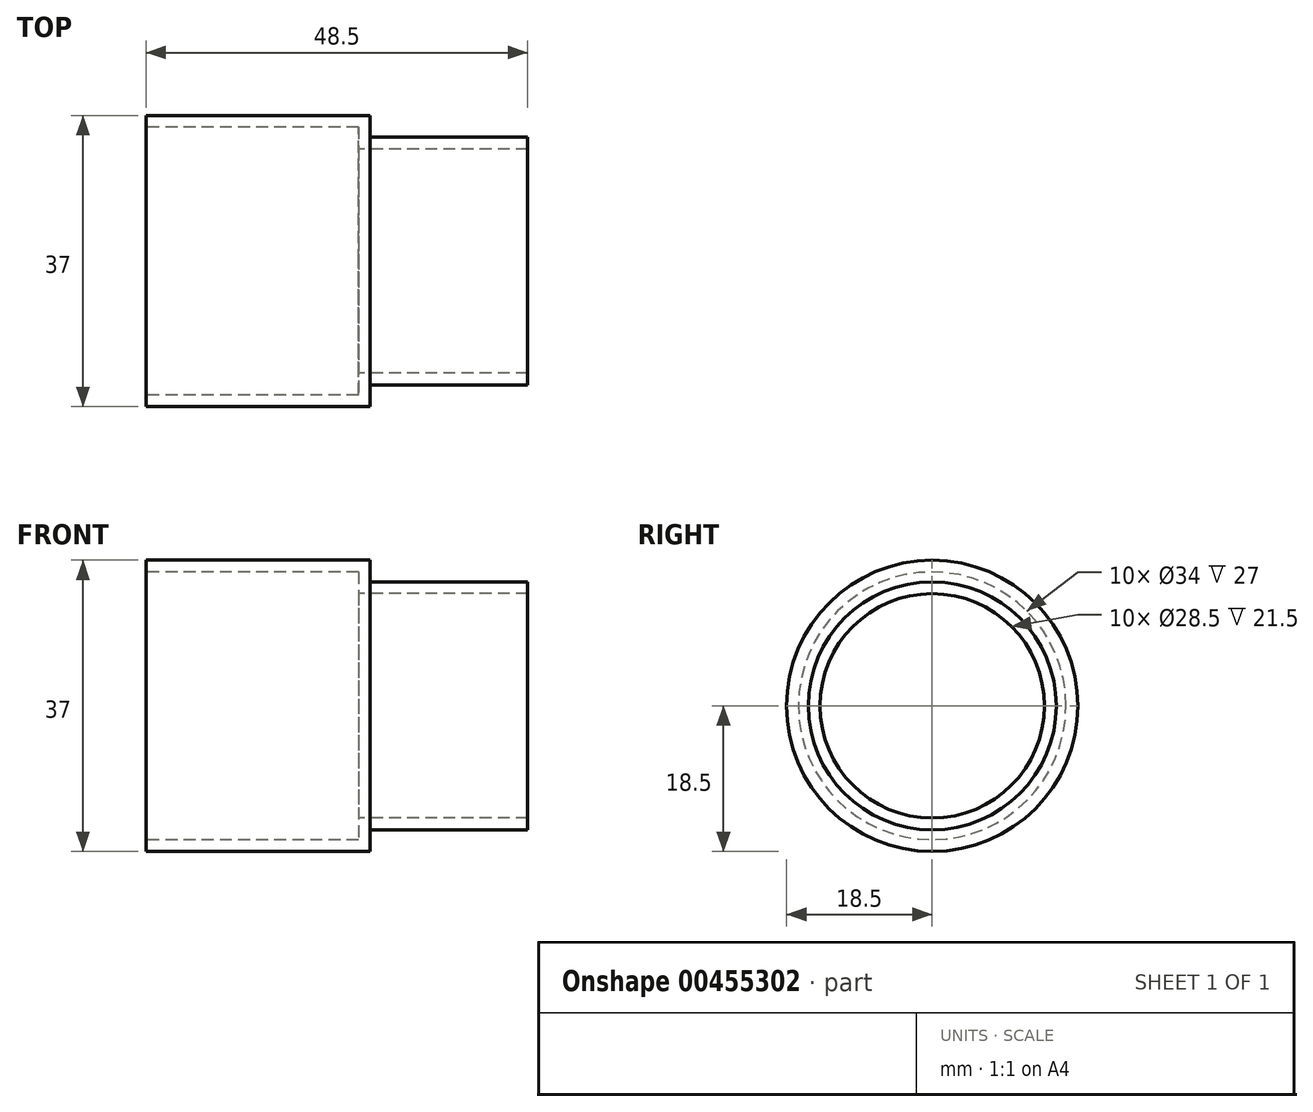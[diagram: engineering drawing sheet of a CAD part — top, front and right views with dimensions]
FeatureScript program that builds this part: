
annotation { "Feature Type Name" : "Feature", "Feature Type Description" : "" }
export const myFeature = defineFeature(function(context is Context, id is Id, definition is map)
    precondition{}
    {
        {
            var Q0;
            Q0=qCreatedBy(makeId("Front.planeOp"),FACE);
            var sketch = newSketch(context, id + "F0", { "sketchPlane" : qUnion([Q0])});
            skLineSegment(sketch, "E0", {"start": v(-28.5, 18.5) * mm, "end": v(0, 18.5) * mm});
            skLineSegment(sketch, "E1", {"start": v(0, 18.5) * mm, "end": v(0, 15.75) * mm});
            skLineSegment(sketch, "E2", {"start": v(0, 15.75) * mm, "end": v(20, 15.75) * mm});
            skLineSegment(sketch, "E3", {"start": v(-28.5, 17) * mm, "end": v(-1.5, 17) * mm});
            skLineSegment(sketch, "E4", {"start": v(-1.5, 17) * mm, "end": v(-1.5, 14.25) * mm});
            skLineSegment(sketch, "E5", {"start": v(-1.5, 14.25) * mm, "end": v(20, 14.25) * mm});
            skLineSegment(sketch, "E6", {"start": v(-28.5, 17) * mm, "end": v(-28.5, 18.5) * mm});
            skLineSegment(sketch, "E7", {"start": v(20, 14.25) * mm, "end": v(20, 15.75) * mm});
            skLineSegment(sketch, "E8", {"start": v(-28.5, 0) * mm, "end": v(20, 0) * mm});
            skSolve(sketch);
        }
        {
            var Q0;
            Q0=makeQuery(id+"F0.imprint","IMPRINT",FACE,{"disambiguationData":[TD([[makeQuery(id+"F0.imprint","IMPRINT",EDGE,{"derivedFrom":sQuery(id+"F0.wireOp",EDGE,"E0")}),-1.0]])]});
            var Q1;
            Q1=sQuery(id+"F0.wireOp",EDGE,"E8");
            revolve(context, id + "F1", {"entities" : qUnion([Q0]), "axis" : qUnion([Q1]), "revolveType" : RevolveType.FULL});
        }
    });
